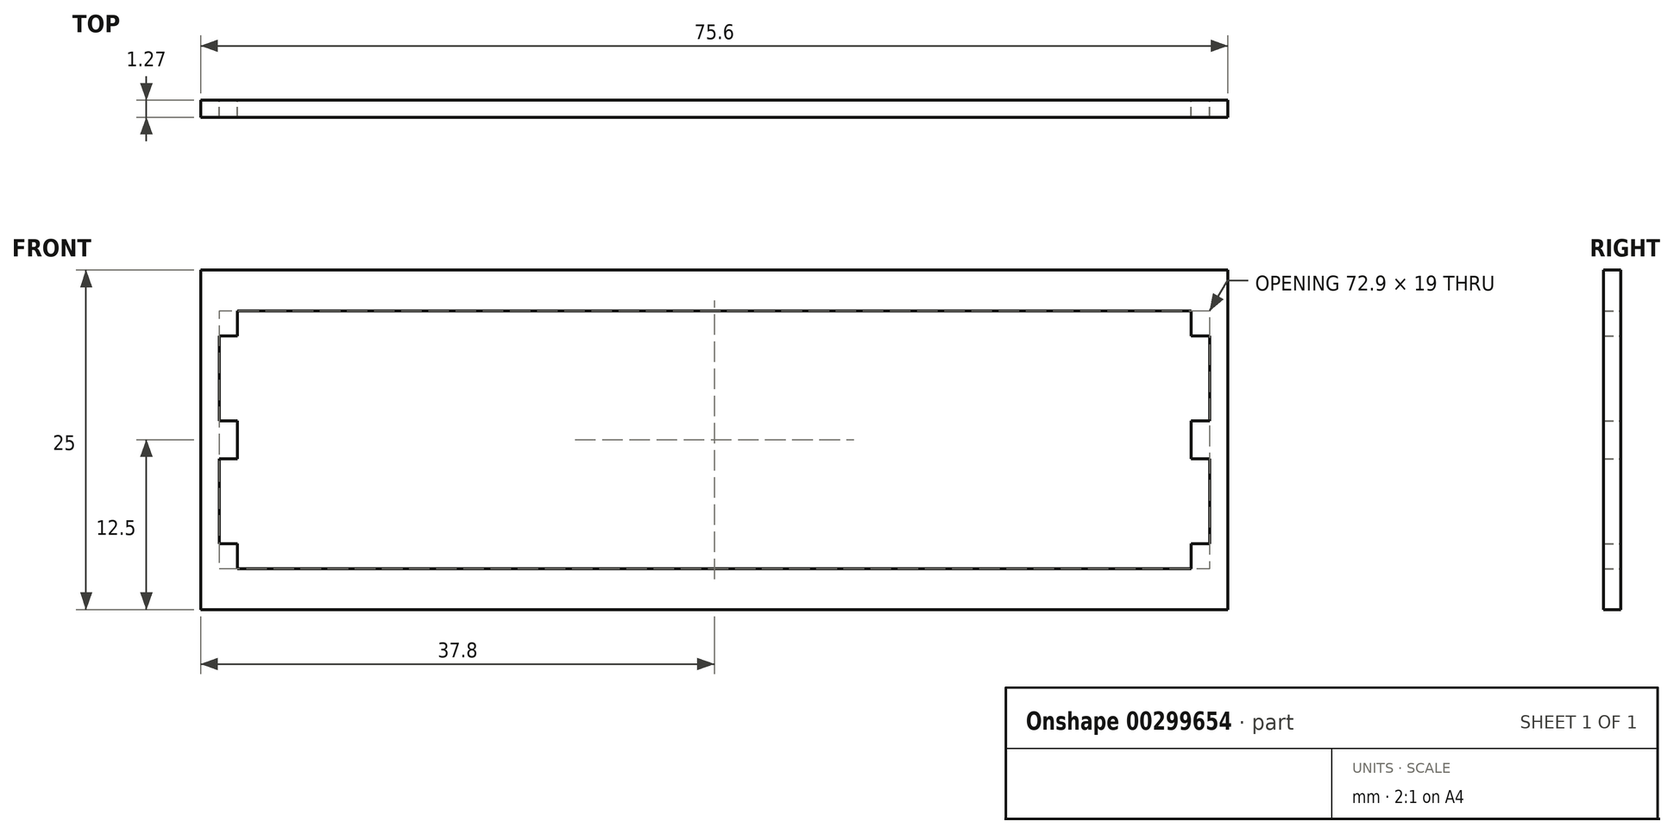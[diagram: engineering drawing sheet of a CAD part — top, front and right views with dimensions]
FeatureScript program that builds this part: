
annotation { "Feature Type Name" : "Feature", "Feature Type Description" : "" }
export const myFeature = defineFeature(function(context is Context, id is Id, definition is map)
    precondition{}
    {
        {
            var Q0;
            Q0=qCreatedBy(makeId("Front.planeOp"),FACE);
            var sketch = newSketch(context, id + "F0", { "sketchPlane" : qUnion([Q0])});
            skLineSegment(sketch, "E0.bottom", {"start": v(37.8, -12.5) * mm, "end": v(-37.8, -12.5) * mm});
            skLineSegment(sketch, "E0.top", {"start": v(37.8, 12.5) * mm, "end": v(-37.8, 12.5) * mm});
            skLineSegment(sketch, "E0.left", {"start": v(37.8, -12.5) * mm, "end": v(37.8, 12.5) * mm});
            skLineSegment(sketch, "E0.right", {"start": v(-37.8, -12.5) * mm, "end": v(-37.8, 12.5) * mm});
            skPoint(sketch, "E0.middle", {"position": v(0, 0) * mm});
            skLineSegment(sketch, "E1.bottom", {"start": v(35.1, -9.5) * mm, "end": v(-35.1, -9.5) * mm});
            skLineSegment(sketch, "E1.top", {"start": v(35.1, 9.5) * mm, "end": v(-35.1, 9.5) * mm});
            skLineSegment(sketch, "E1.left", {"start": v(35.1, -9.5) * mm, "end": v(35.1, 9.5) * mm});
            skLineSegment(sketch, "E1.right", {"start": v(-35.1, -9.5) * mm, "end": v(-35.1, 9.5) * mm});
            skLineSegment(sketch, "E2.bottom", {"start": v(-37.8, 12.5) * mm, "end": v(-36.45, 12.5) * mm, "construction": true});
            skLineSegment(sketch, "E2.top", {"start": v(-37.8, 7.65) * mm, "end": v(-36.45, 7.65) * mm, "construction": true});
            skLineSegment(sketch, "E2.left", {"start": v(-37.8, 12.5) * mm, "end": v(-37.8, 7.65) * mm, "construction": true});
            skLineSegment(sketch, "E2.right", {"start": v(-36.45, 12.5) * mm, "end": v(-36.45, 7.65) * mm, "construction": true});
            skLineSegment(sketch, "E3.bottom", {"start": v(-36.45, 7.65) * mm, "end": v(36.45, 7.65) * mm});
            skLineSegment(sketch, "E3.top", {"start": v(-36.45, 1.4) * mm, "end": v(36.45, 1.4) * mm});
            skLineSegment(sketch, "E3.left", {"start": v(-36.45, 7.65) * mm, "end": v(-36.45, 1.4) * mm});
            skLineSegment(sketch, "E3.right", {"start": v(36.45, 7.65) * mm, "end": v(36.45, 1.4) * mm});
            skLineSegment(sketch, "E4.bottom", {"start": v(-37.8, -12.5) * mm, "end": v(-36.45, -12.5) * mm, "construction": true});
            skLineSegment(sketch, "E4.top", {"start": v(-37.8, -7.65) * mm, "end": v(-36.45, -7.65) * mm, "construction": true});
            skLineSegment(sketch, "E4.left", {"start": v(-37.8, -12.5) * mm, "end": v(-37.8, -7.65) * mm, "construction": true});
            skLineSegment(sketch, "E4.right", {"start": v(-36.45, -12.5) * mm, "end": v(-36.45, -7.65) * mm, "construction": true});
            skLineSegment(sketch, "E5.bottom", {"start": v(-36.45, -7.65) * mm, "end": v(36.45, -7.65) * mm});
            skLineSegment(sketch, "E5.top", {"start": v(-36.45, -1.4) * mm, "end": v(36.45, -1.4) * mm});
            skLineSegment(sketch, "E5.left", {"start": v(-36.45, -7.65) * mm, "end": v(-36.45, -1.4) * mm});
            skLineSegment(sketch, "E5.right", {"start": v(36.45, -7.65) * mm, "end": v(36.45, -1.4) * mm});
            skSolve(sketch);
        }
        {
            var Q0;
            Q0=makeQuery(id+"F0.imprint","IMPRINT",FACE,{"disambiguationData":[TD([[makeQuery(id+"F0.imprint","IMPRINT",EDGE,{"derivedFrom":sQuery(id+"F0.wireOp",EDGE,"E0.bottom")}),-1.0]])]});
            extrude(context, id + "F1", {"entities" : qUnion([Q0]), "depth" : 1.27 * mm});
        }
    });
